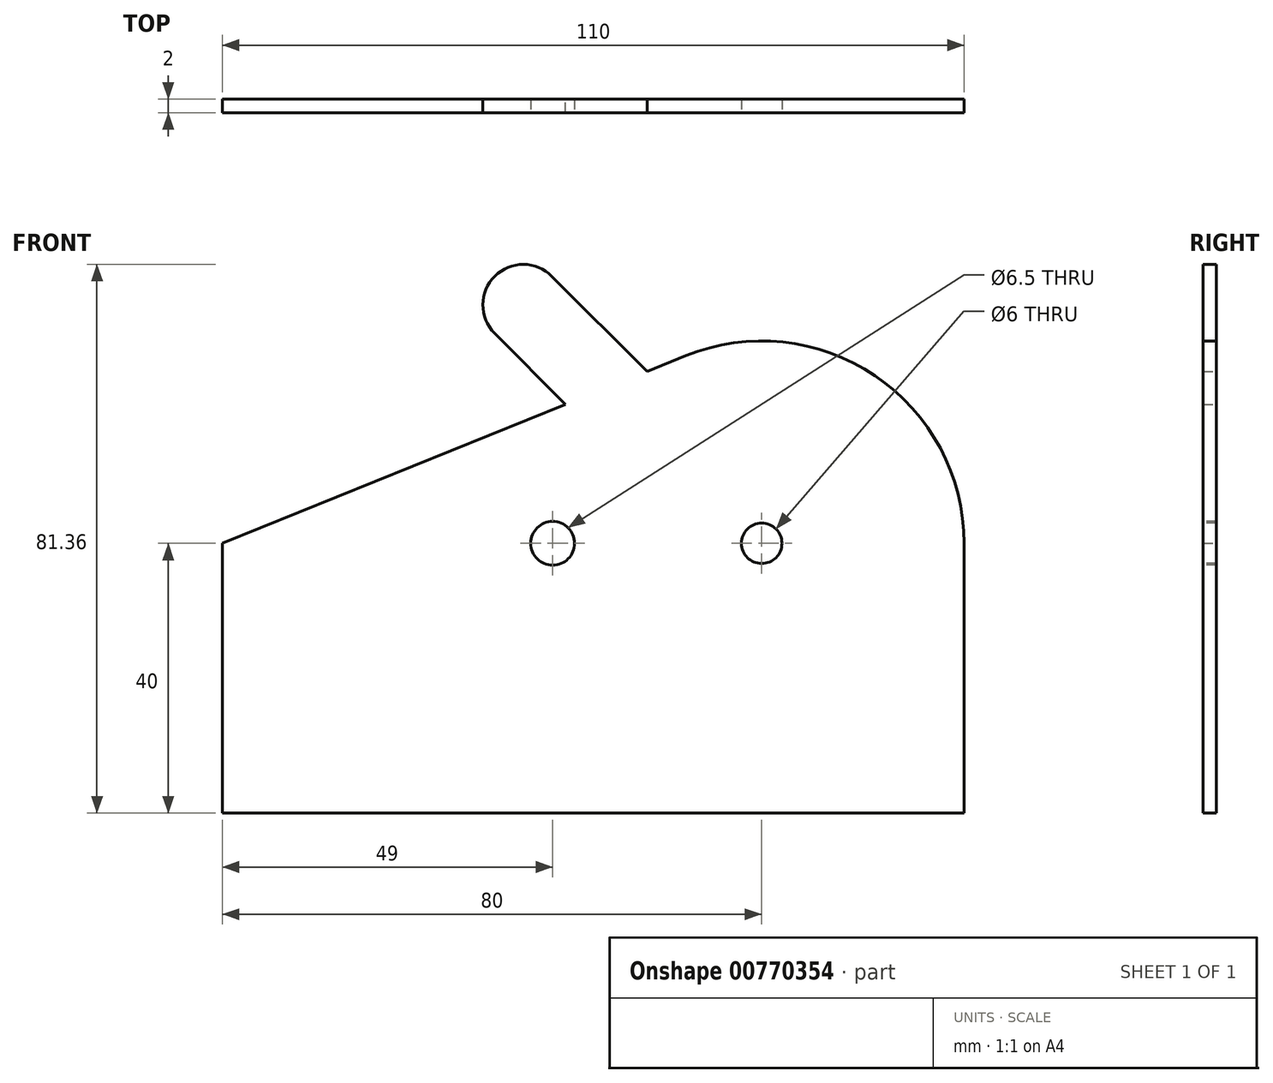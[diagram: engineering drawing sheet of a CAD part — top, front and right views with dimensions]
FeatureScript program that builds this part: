
annotation { "Feature Type Name" : "Feature", "Feature Type Description" : "" }
export const myFeature = defineFeature(function(context is Context, id is Id, definition is map)
    precondition{}
    {
        {
            var Q0;
            Q0=qCreatedBy(makeId("Front.planeOp"),FACE);
            var sketch = newSketch(context, id + "F0", { "sketchPlane" : qUnion([Q0])});
            skLineSegment(sketch, "E0", {"start": v(-11.25, 27.81) * mm, "end": v(-80, 0) * mm});
            skLineSegment(sketch, "E1", {"start": v(-80, 0) * mm, "end": v(-80, -40) * mm});
            skLineSegment(sketch, "E2", {"start": v(-80, -40) * mm, "end": v(30, -40) * mm});
            skLineSegment(sketch, "E3", {"start": v(30, -40) * mm, "end": v(30, 0) * mm});
            skArc(sketch, "E4", {"start": v(-11.25, 27.81) * mm, "mid": v(16.77, 24.87) * mm, "end": v(30, 0) * mm});
            skCircle(sketch, "E5", {"center": v(-31, 0) * mm, "radius": 6 * mm, "construction": true});
            skCircle(sketch, "E6", {"center": v(0, 0) * mm, "radius": 25 * mm, "construction": true});
            skLineSegment(sketch, "E7", {"start": v(-17, 25.48) * mm, "end": v(-31.11, 39.6) * mm});
            skLineSegment(sketch, "E8", {"start": v(-29.08, 20.6) * mm, "end": v(-39.6, 31.11) * mm});
            skArc(sketch, "E9", {"start": v(-39.6, 31.11) * mm, "mid": v(-39.6, 39.6) * mm, "end": v(-31.11, 39.6) * mm});
            skLineSegment(sketch, "E10", {"start": v(-35.36, 35.36) * mm, "end": v(0, 0) * mm, "construction": true});
            skSolve(sketch);
        }
        {
            var Q0;
            Q0=makeQuery(id+"F0.imprint","IMPRINT",FACE,{"disambiguationData":[TD([[makeQuery(id+"F0.imprint","IMPRINT",EDGE,{"derivedFrom":sQuery(id+"F0.wireOp",EDGE,"E0")}),1.0]])]});
            extrude(context, id + "F1", {"entities" : qUnion([Q0]), "endBound" : BoundingType.SYMMETRIC, "depth" : 2 * mm, "offsetDistance" : 25 * mm});
        }
        {
            var Q0;
            Q0=makeQuery(id+"F1.opExtrude","CAP_FACE",FACE,{"disambiguationData":[OSD([sQuery(id+"F0.wireOp",EDGE,"E0"),sQuery(id+"F0.wireOp",EDGE,"E1"),sQuery(id+"F0.wireOp",EDGE,"E2"),sQuery(id+"F0.wireOp",EDGE,"E3"),sQuery(id+"F0.wireOp",EDGE,"E4")])],"isStart":false});
            var sketch = newSketch(context, id + "F2", { "sketchPlane" : qUnion([Q0])});
            skCircle(sketch, "E11", {"center": v(0, 0) * mm, "radius": 3 * mm});
            skCircle(sketch, "E12", {"center": v(-31, 0) * mm, "radius": 3.25 * mm});
            skSolve(sketch);
        }
        {
            var Q0;
            Q0 = qSketchRegion(id + "F2", true);
            extrude(context, id + "F3", {"entities" : qUnion([Q0]), "operationType" : NewBodyOperationType.REMOVE, "endBound" : BoundingType.THROUGH_ALL, "oppositeDirection" : true, "depth" : 25 * mm, "offsetDistance" : 25 * mm});
        }
        {
            var Q0;
            {var subQ0=sQuery(id+"F0.wireOp",EDGE,"E7");Q0=makeQuery(id+"F0.imprint","IMPRINT",FACE,{"disambiguationData":[TD([[makeQuery(id+"F0.imprint","IMPRINT",EDGE,{"derivedFrom":subQ0}),1.0]])]});}
            extrude(context, id + "F4", {"entities" : qUnion([Q0]), "operationType" : NewBodyOperationType.ADD, "endBound" : BoundingType.SYMMETRIC, "depth" : 2 * mm, "offsetDistance" : 25 * mm});
        }
    });
